# Revit family: 3966000
name_source: partatom
category: Plumbing Fixtures
revit_build: Autodesk Revit 2016 (Build: 20150714_1515(x64)
units: mm (PartAtom-declared; Revit-internal decimal feet)

## family parameters
Always vertical = No
Cut with Voids When Loaded = Yes
OmniClass Number = 23.45.05.14.14
OmniClass Title = Sinks/Lavatories
Part Type = Normal
Room Calculation Point = No
Round Connector Dimension = Use Diameter
Shared = Yes
Work Plane-Based = Yes

## types (1)
- 39660000
    ADA Compliant = Yes
    Assembly Code = D2010310
    Basin Shape = Rectangular
    Bowl Depth = 15 3/8"
    Bowl Width = 19 3/4"
    CW Connection = Yes
    CWFU = 1.5
    Cold Water Connection Diameter = 3/8"
    Cold Water Connection Height = 13 1/4"
    Cold Water Connection Width = 2"
    Default Elevation = 0"
    Depth = 16 3/16"
    Description = EUROCUBE DROP-IN/ UNDER COUNTER LAVATORY
    Finish = Fine Fire Clay-Grohe-000-Alpine White
    HW Connection = Yes
    HWFU = 1.5
    Height = 7"
    Hot Water Connection Diameter = 0"
    Hot Water Connection Height = 13 1/4"
    Hot Water Connection Width = 2"
    IAPMO Compliance = cUPC
    Installation Type = Dual mount
    Manufacturer = Grohe
    Material = Fine Fire Clay-Grohe-000-Alpine White
    Model = 39660000
    Price = Prices may vary. Please consult Manufacturer Representative for most up-to-date price list.
    URL = https://www.grohe.us
    Vent Connection = No
    WFU = 2
    Wall To Back of Basin = 4"
    Warranty Documentation Link = www.grohe.us/en_us/our-service/warranty/
    Waste Connection = Yes
    Waste Connection Diameter = 1 1/4"
    Waste Connection Height = 14 1/4"
    Width = 21"

## geometry (parser evidence)
native form markers: Sweep x2
no freeform markers — native parametric forms only
